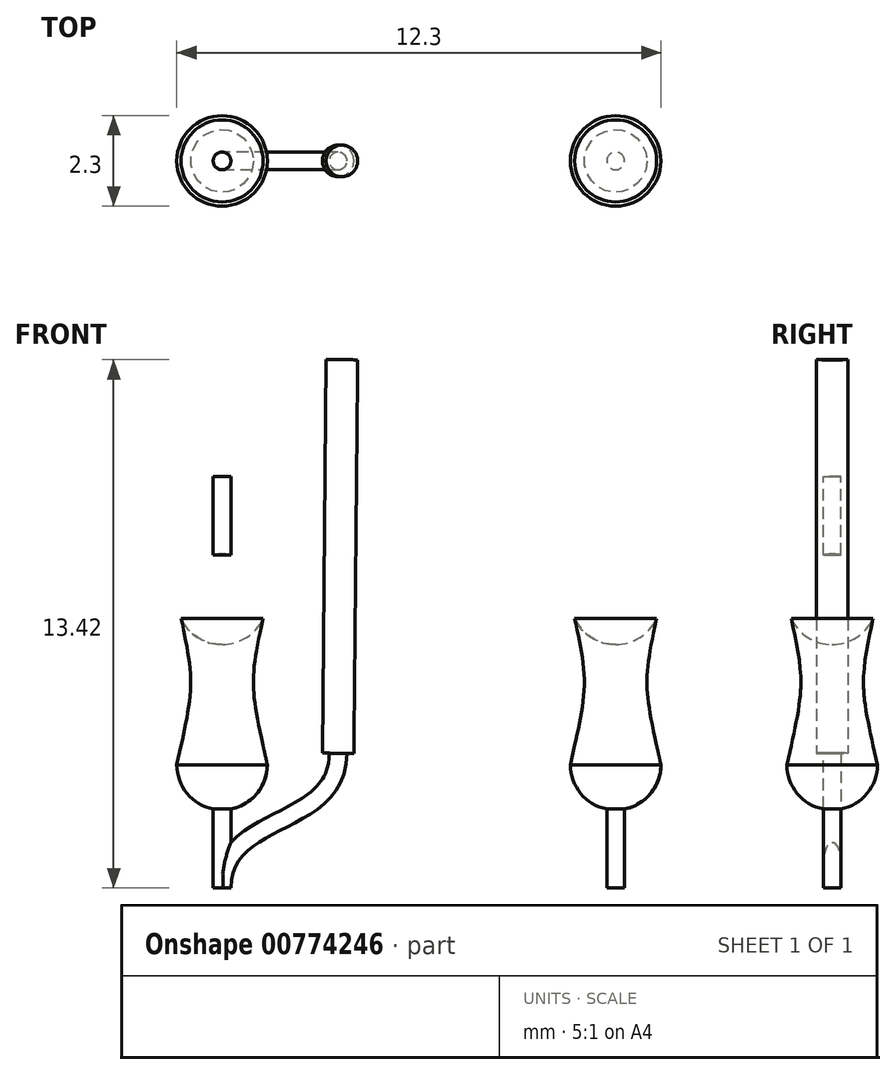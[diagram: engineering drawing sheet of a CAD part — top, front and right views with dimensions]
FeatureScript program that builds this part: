
annotation { "Feature Type Name" : "Feature", "Feature Type Description" : "" }
export const myFeature = defineFeature(function(context is Context, id is Id, definition is map)
    precondition{}
    {
        {
            var Q0;
            Q0=qCreatedBy(makeId("Front.planeOp"),FACE);
            var sketch = newSketch(context, id + "F0", { "sketchPlane" : qUnion([Q0])});
            skLineSegment(sketch, "E0", {"start": v(0, 12.06) * mm, "end": v(0, -5.23) * mm});
            skLineSegment(sketch, "E1", {"start": v(0, -5.23) * mm, "end": v(-0.22, -5.23) * mm});
            skLineSegment(sketch, "E2", {"start": v(-0.22, -5.23) * mm, "end": v(-0.22, -3.23) * mm});
            skArc(sketch, "E3", {"start": v(0, -0.95) * mm, "mid": v(-1.15, -2.1) * mm, "end": v(0, -3.25) * mm});
            skArc(sketch, "E4.MirrorC", {"start": v(0, 0.95) * mm, "mid": v(-1.15, 2.1) * mm, "end": v(0, 3.25) * mm});
            skLineSegment(sketch, "E5.MirrorCS", {"start": v(-0.22, 5.23) * mm, "end": v(-0.22, 3.23) * mm});
            skLineSegment(sketch, "E6.MirrorCS", {"start": v(0, 5.23) * mm, "end": v(-0.22, 5.23) * mm});
            skFitSpline(sketch, "E7", {"points": [v(-1.15, 2.1) * mm, v(-1.15, -2.1) * mm], "startDerivative": vector(1.42, -6.3) * mm, "endDerivative": vector(-1.42, -6.3) * mm});
            skSolve(sketch);
        }
        {
            var Q0;
            {var subQ4=sQuery(id+"F0.wireOp",EDGE,"E5.MirrorCS");Q0=makeQuery(id+"F0.imprint","IMPRINT",FACE,{"disambiguationData":[TD([[makeQuery(id+"F0.imprint","IMPRINT",EDGE,{"derivedFrom":subQ4}),1.0]])]});}
            var Q1;
            {var subQ0=sQuery(id+"F0.wireOp",EDGE,"E4.MirrorC");var subQ1=sQuery(id+"F0.wireOp",EDGE,"E0");var subQ6=makeQuery(id+"F0.imprint","INTERSECT",VERTEX,{"disambiguationData":[OD(0.0)],"derivedFrom":[subQ1,subQ0]});Q1=makeQuery(id+"F0.imprint","IMPRINT",FACE,{"disambiguationData":[TD([[makeQuery(id+"F0.imprint","IMPRINT",EDGE,{"disambiguationData":[TD([[subQ6,1.0]])],"derivedFrom":subQ1}),-1.0]])]});}
            var Q2;
            {var subQ0=sQuery(id+"F0.wireOp",EDGE,"E3");var subQ1=sQuery(id+"F0.wireOp",EDGE,"E0");var subQ2=makeQuery(id+"F0.imprint","INTERSECT",VERTEX,{"disambiguationData":[OD(0.0)],"derivedFrom":[subQ1,subQ0]});Q2=makeQuery(id+"F0.imprint","IMPRINT",FACE,{"disambiguationData":[TD([[makeQuery(id+"F0.imprint","IMPRINT",EDGE,{"disambiguationData":[TD([[subQ2,1.0]])],"derivedFrom":subQ1}),-1.0]])]});}
            var Q3;
            {var subQ0=sQuery(id+"F0.wireOp",EDGE,"E3");var subQ2=sQuery(id+"F0.wireOp",EDGE,"E0");var subQ6=makeQuery(id+"F0.imprint","INTERSECT",VERTEX,{"disambiguationData":[OD(0.0)],"derivedFrom":[subQ2,subQ0]});Q3=makeQuery(id+"F0.imprint","IMPRINT",FACE,{"disambiguationData":[TD([[makeQuery(id+"F0.imprint","IMPRINT",EDGE,{"disambiguationData":[TD([[subQ6,-1.0]])],"derivedFrom":subQ2}),-1.0]])]});}
            var Q4;
            {var subQ0=sQuery(id+"F0.wireOp",EDGE,"E1");Q4=makeQuery(id+"F0.imprint","IMPRINT",FACE,{"disambiguationData":[TD([[makeQuery(id+"F0.imprint","IMPRINT",EDGE,{"derivedFrom":subQ0}),-1.0]])]});}
            var Q5;
            Q5=sQuery(id+"F0.wireOp",EDGE,"E0");
            revolve(context, id + "F1", {"surfaceOperationType" : NewSurfaceOperationType.NEW, "entities" : qUnion([Q0, Q1, Q2, Q3, Q4]), "axis" : qUnion([Q5]), "revolveType" : RevolveType.FULL});
        }
        {
            var Q0;
            Q0=makeQuery(id+"F1.opRevolve","SWEPT_BODY",BODY,{"disambiguationData":[OSD([sQuery(id+"F0.wireOp",EDGE,"E0"),sQuery(id+"F0.wireOp",EDGE,"E1"),sQuery(id+"F0.wireOp",EDGE,"E2"),sQuery(id+"F0.wireOp",EDGE,"E3"),sQuery(id+"F0.wireOp",EDGE,"E4.MirrorC"),sQuery(id+"F0.wireOp",EDGE,"E5.MirrorCS"),sQuery(id+"F0.wireOp",EDGE,"E6.MirrorCS"),sQuery(id+"F0.wireOp",EDGE,"E7")])]});
            transform(context, id + "F2", {"entities" : qUnion([Q0]), "transformType" : TransformType.TRANSLATION_3D, "dx" : 10 * mm, "dy" : 0 * mm, "dz" : 0 * mm, "makeCopy" : true});
        }
        {
            var Q0;
            Q0=qCreatedBy(makeId("Front.planeOp"),FACE);
            var sketch = newSketch(context, id + "F3", { "sketchPlane" : qUnion([Q0])});
            skFitSpline(sketch, "E8", {"points": [v(0, -5.23) * mm, v(2.95, -1.8) * mm], "startDerivative": vector(0, 5.77) * mm, "endDerivative": vector(0.06, 5.81) * mm});
            skSolve(sketch);
        }
        {
            var Q0;
            Q0=makeQuery(id+"F1.opRevolve","SWEPT_FACE",FACE,{"disambiguationData":[OSD([sQuery(id+"F0.wireOp",EDGE,"E1")])]});
            var Q1;
            Q1=sQuery(id+"F3.wireOp",EDGE,"E8");
            sweep(context, id + "F4", {"operationType" : NewBodyOperationType.ADD, "profiles" : qUnion([Q0]), "path" : qUnion([Q1])});
        }
        {
            var Q0;
            Q0=makeQuery(id+"F4.opSweep","CAP_FACE",FACE,{"disambiguationData":[OSD([sQuery(id+"F0.wireOp",EDGE,"E1"),sQuery(id+"F3.wireOp",VERTEX,"E8.end")])],"isStart":true});
            var sketch = newSketch(context, id + "F5", { "sketchPlane" : qUnion([Q0])});
            skCircle(sketch, "E9", {"center": v(2.97, 0) * mm, "radius": 0.4 * mm});
            skSolve(sketch);
        }
        {
            var Q0;
            Q0=makeQuery(id+"F5.imprint","IMPRINT",FACE,{"disambiguationData":[TD([[makeQuery(id+"F5.imprint","IMPRINT",EDGE,{"derivedFrom":sQuery(id+"F5.wireOp",EDGE,"E9")}),1.0]])]});
            var Q1;
            Q1=makeQuery(id+"F5.imprint","IMPRINT",FACE,{"disambiguationData":[TD([[makeQuery(id+"F5.imprint","IMPRINT",EDGE,{"derivedFrom":makeQuery(id+"F4.opSweep","CAP_EDGE",EDGE,{"disambiguationData":[OSD([sQuery(id+"F0.wireOp",EDGE,"E1"),sQuery(id+"F0.wireOp",EDGE,"E2"),sQuery(id+"F3.wireOp",VERTEX,"E8.end")])],"isStart":true})}),-1.0]])]});
            extrude(context, id + "F6", {"entities" : qUnion([Q0, Q1]), "operationType" : NewBodyOperationType.ADD, "depth" : 10 * mm, "offsetDistance" : 25 * mm});
        }
    });
